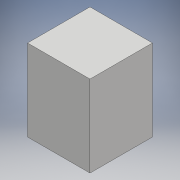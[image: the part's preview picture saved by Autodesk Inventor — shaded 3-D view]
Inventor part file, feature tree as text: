
AUTODESK INVENTOR PART (.ipt)
format: ipt  version: 2017 (Build 210142000, 142)  size: 84,480 bytes
history: native  units: mm
features: extrude x1, sketch x1
ambient origin geometry x8: Origin, YZ Plane, XZ Plane, XY Plane, X Axis, Y Axis, Z Axis, Center Point
bodies: Solid1 (feature_tree)
feature tree (2):
  extrude  "Extrusion1"  Depth=115.0mm
  sketch  "Sketch1"  dims[d0=115.0mm d1=115.0mm d2=150.0mm d3=0.0mm]
